FCSTD DOCUMENT  (FreeCAD 1.0R39319 (Git))
Label: StopNU_bottom
License: Creative Commons Attribution 4.0
LicenseURL: https://creativecommons.org/licenses/by/4.0/
objects: TechDraw::DrawViewDimension×7, Sketcher::SketchObject×1, TechDraw::DrawSVGTemplate×1, TechDraw::DrawProjGroupItem×1, TechDraw::DrawPage×1
note: 15 computed .brp shape members not serialized (recipe doc carries the construction recipe); baked Part::Feature solids carry a one-line shape summary decoded from their .brp

FEATURE [Sketcher::SketchObject] Sketch
  ArcFitTolerance = 1e-06
  FullyConstrained = true
  MakeInternals = false
  sketch-geometry (7):
    g0: Circle CenterX=-52 CenterY=-84 CenterZ=0 NormalX=0 NormalY=0 NormalZ=1 AngleXU=0 Radius=5
    g1: Circle CenterX=52 CenterY=-84 CenterZ=0 NormalX=0 NormalY=0 NormalZ=1 AngleXU=0 Radius=5
    g2: Circle CenterX=-102.5 CenterY=-11 CenterZ=0 NormalX=0 NormalY=0 NormalZ=1 AngleXU=0 Radius=5
    g3: Circle CenterX=102.5 CenterY=-11 CenterZ=0 NormalX=0 NormalY=0 NormalZ=1 AngleXU=0 Radius=5
    g4: LineSegment StartX=-122.5 StartY=0 StartZ=0 EndX=122.5 EndY=-3e-14 EndZ=0
    g5: ArcOfCircle CenterX=0 CenterY=0 CenterZ=0 NormalX=0 NormalY=0 NormalZ=1 AngleXU=0 Radius=122.5 StartAngle=3.14159 EndAngle=6.28319
    g6: Circle CenterX=0 CenterY=-45 CenterZ=0 NormalX=0 NormalY=0 NormalZ=1 AngleXU=0 Radius=32.5
  constraints (19):
    c: Diameter(g0) = 10
    c: Equal(g2,g0)
    c: Equal(g0,g1)
    c: Equal(g1,g3)
    c: Symmetric(g2,g3,g-2)
    c: DistanceY(g2,g-1) = 11
    c: DistanceY(g0) = -84
    c: Symmetric(g1,g0,g-2)
    c: DistanceX(g0,g1) = 104
    c: DistanceX(g2,g3) = 205
    c: PointOnObject(g4,g-1)
    c: PointOnObject(g4,g-1)
    c: Coincident(g5,g-1)
    c: Coincident(g5,g4)
    c: Coincident(g5,g4)
    c: Diameter(g6) = 65
    c: PointOnObject(g6,g-2)
    c: DistanceY(g6) = -45
    c: DistanceX(g3,g4) = 20
FEATURE [TechDraw::DrawSVGTemplate] Template
  EditableTexts = approval_person=no-one; creator=jhaand; date_of_issue=2025-08-31; document_type=Assembly Drawing; general_tolerances=ISO 2768-m; identification_number=DN; language_code=EN; part_material=STOPNU_onderkant; revision_index=AAA; sheet_number=1 / 1; sheet_scale=1 : 1; title=Unnamed
  Height = 297
  Orientation = 1
  Template = <userpath>/storage/Techdraw_local/Templates/A3_Landscape_ISO5457_minimal.svg
  Width = 420
FEATURE [TechDraw::DrawProjGroupItem] View
  CoarseView = false
  Direction = (0,0,1)
  Focus = 100
  HardHidden = false
  IsoCount = 0
  IsoHidden = false
  IsoVisible = false
  LockPosition = false
  Perspective = false
  Rotation = 0
  RotationVector = (1,0,0)
  ScaleType = 0
  ScrubCount = 1
  SeamHidden = false
  SeamVisible = false
  SmoothHidden = false
  SmoothVisible = true
  Source = -> [Sketch]
  Type = 0
  X = 210
  XDirection = (1,0,0)
  Y = 148.5
FEATURE [TechDraw::DrawViewDimension] Dimension
  AngleOverride = false
  Arbitrary = false
  ArbitraryTolerances = false
  BoxCorners = (2) [(-122.5,-61.25,0),(122.5,61.25,0)]
  EqualTolerance = true
  ExtensionAngle = 0
  FormatSpec = %.2w
  FormatSpecOverTolerance = %+.2w
  FormatSpecUnderTolerance = %+.2w
  Inverted = false
  LineAngle = 0
  LockPosition = false
  MeasureType = 1
  OverTolerance = 0
  References2D = -> [View]
  Rotation = 0
  ScaleType = 0
  TheoreticalExact = false
  Type = 2
  UnderTolerance = 0
  X = -95.4519
  Y = 55.75
FEATURE [TechDraw::DrawViewDimension] Dimension001
  AngleOverride = false
  Arbitrary = false
  ArbitraryTolerances = false
  BoxCorners = (2) [(-122.5,-61.25,0),(122.5,61.25,0)]
  EqualTolerance = true
  ExtensionAngle = 0
  FormatSpec = %.2w
  FormatSpecOverTolerance = %+.2w
  FormatSpecUnderTolerance = %+.2w
  Inverted = false
  LineAngle = 0
  LockPosition = false
  MeasureType = 1
  OverTolerance = 0
  References2D = -> [View]
  Rotation = 0
  ScaleType = 0
  TheoreticalExact = false
  Type = 1
  UnderTolerance = 0
  X = -91.6054
  Y = 82.375
FEATURE [TechDraw::DrawViewDimension] Dimension002
  AngleOverride = false
  Arbitrary = false
  ArbitraryTolerances = false
  BoxCorners = (2) [(-122.5,-61.25,0),(122.5,61.25,0)]
  EqualTolerance = true
  ExtensionAngle = 0
  FormatSpec = %.2w
  FormatSpecOverTolerance = %+.2w
  FormatSpecUnderTolerance = %+.2w
  Inverted = false
  LineAngle = 0
  LockPosition = false
  MeasureType = 1
  OverTolerance = 0
  References2D = -> [View]
  Rotation = 0
  ScaleType = 0
  TheoreticalExact = false
  Type = 2
  UnderTolerance = 0
  X = -49.2268
  Y = 38.75
FEATURE [TechDraw::DrawViewDimension] Dimension003
  AngleOverride = false
  Arbitrary = false
  ArbitraryTolerances = false
  BoxCorners = (2) [(-122.5,-61.25,0),(122.5,61.25,0)]
  EqualTolerance = true
  ExtensionAngle = 0
  FormatSpec = ⌀%.2w
  FormatSpecOverTolerance = %+.2w
  FormatSpecUnderTolerance = %+.2w
  Inverted = false
  LineAngle = 0
  LockPosition = false
  MeasureType = 1
  OverTolerance = 0
  References2D = -> [View]
  Rotation = 0
  ScaleType = 0
  TheoreticalExact = false
  Type = 5
  UnderTolerance = 0
  X = 44.016
  Y = 46.7768
FEATURE [TechDraw::DrawViewDimension] Dimension004
  AngleOverride = false
  Arbitrary = false
  ArbitraryTolerances = false
  BoxCorners = (2) [(-122.5,-61.25,0),(122.5,61.25,0)]
  EqualTolerance = true
  ExtensionAngle = 0
  FormatSpec = %.2w
  FormatSpecOverTolerance = %+.2w
  FormatSpecUnderTolerance = %+.2w
  Inverted = false
  LineAngle = 0
  LockPosition = false
  MeasureType = 1
  OverTolerance = 0
  References2D = -> [View]
  Rotation = 0
  ScaleType = 0
  TheoreticalExact = false
  Type = 1
  UnderTolerance = 0
  X = -7.55509
  Y = -22.1266
FEATURE [TechDraw::DrawViewDimension] Dimension005
  AngleOverride = false
  Arbitrary = false
  ArbitraryTolerances = false
  BoxCorners = (2) [(-122.5,-61.25,0),(122.5,61.25,0)]
  EqualTolerance = true
  ExtensionAngle = 0
  FormatSpec = %.2w
  FormatSpecOverTolerance = %+.2w
  FormatSpecUnderTolerance = %+.2w
  Inverted = false
  LineAngle = 0
  LockPosition = false
  MeasureType = 1
  OverTolerance = 0
  References2D = -> [View]
  Rotation = 0
  ScaleType = 0
  TheoreticalExact = false
  Type = 0
  UnderTolerance = 0
  X = -74.5506
  Y = 27.7889
FEATURE [TechDraw::DrawViewDimension] Dimension006
  AngleOverride = false
  Arbitrary = false
  ArbitraryTolerances = false
  BoxCorners = (2) [(-122.5,-61.25,0),(122.5,61.25,0)]
  EqualTolerance = true
  ExtensionAngle = 0
  FormatSpec = %.2w
  FormatSpecOverTolerance = %+.2w
  FormatSpecUnderTolerance = %+.2w
  Inverted = false
  LineAngle = 0
  LockPosition = false
  MeasureType = 1
  OverTolerance = 0
  References2D = -> [View]
  Rotation = 0
  ScaleType = 0
  TheoreticalExact = false
  Type = 0
  UnderTolerance = 0
  X = -81.8578
  Y = 10.5624
FEATURE [TechDraw::DrawPage] Page
  KeepUpdated = true
  NextBalloonIndex = 1
  ProjectionType = 1
  Template = -> Template
  Views = -> [View,Dimension,Dimension001,Dimension002,Dimension003,Dimension004,Dimension005,Dimension006]
